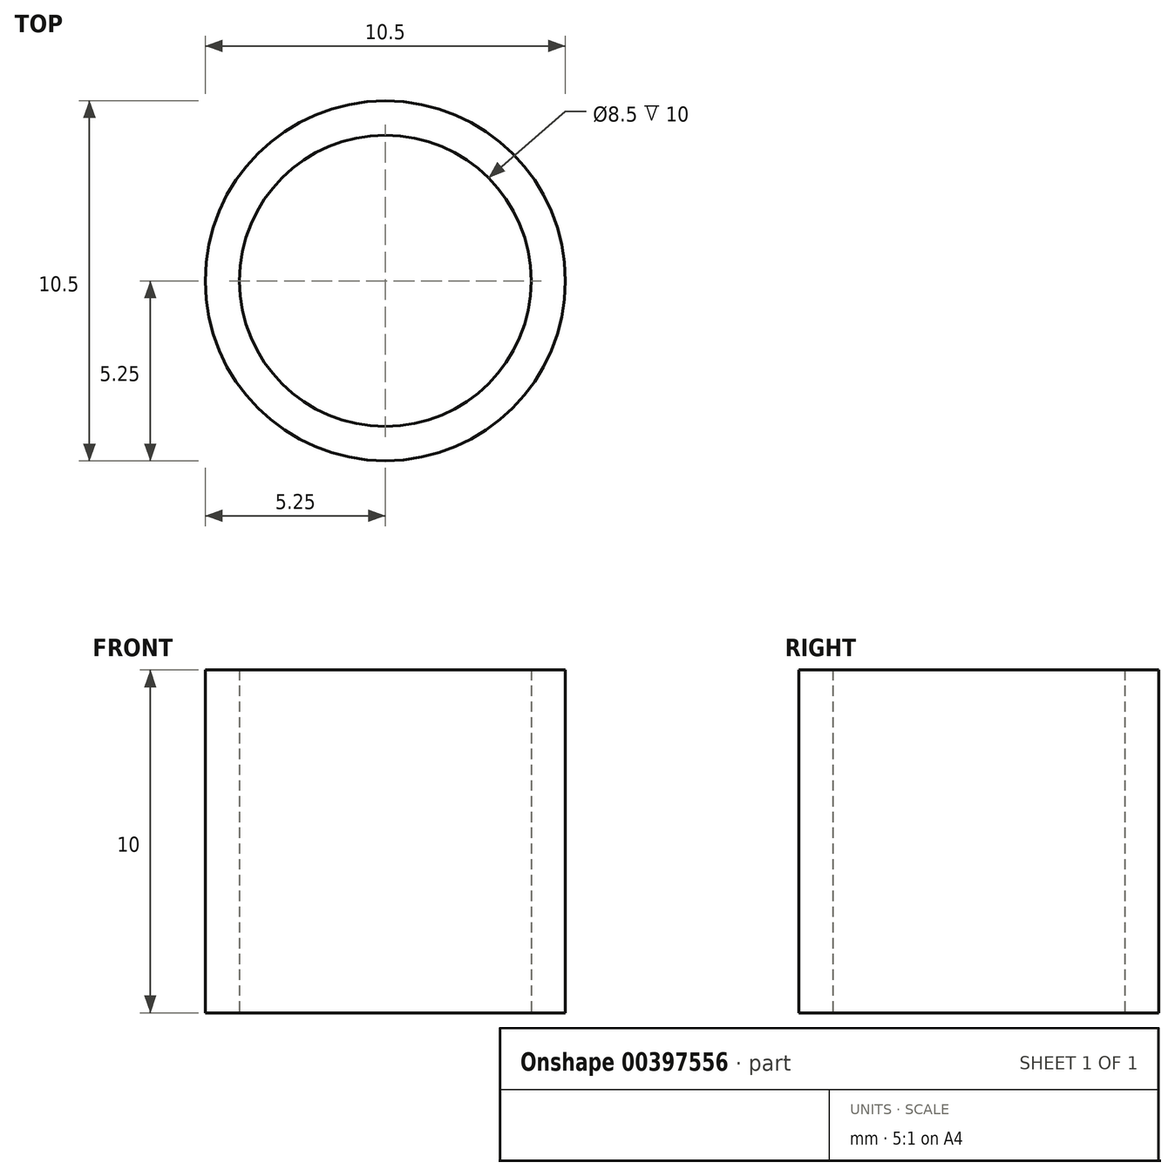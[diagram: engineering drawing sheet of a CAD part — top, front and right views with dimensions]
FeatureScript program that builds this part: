
annotation { "Feature Type Name" : "Feature", "Feature Type Description" : "" }
export const myFeature = defineFeature(function(context is Context, id is Id, definition is map)
    precondition{}
    {
        {
            var Q0;
            Q0=qCreatedBy(makeId("Top.planeOp"),FACE);
            var sketch = newSketch(context, id + "F0", { "sketchPlane" : qUnion([Q0])});
            skCircle(sketch, "E0", {"center": v(0, 0) * mm, "radius": 5.25 * mm});
            skCircle(sketch, "E1", {"center": v(0, 0) * mm, "radius": 4.25 * mm});
            skSolve(sketch);
        }
        {
            var Q0;
            Q0=makeQuery(id+"F0.imprint","IMPRINT",FACE,{"disambiguationData":[TD([[makeQuery(id+"F0.imprint","IMPRINT",EDGE,{"derivedFrom":sQuery(id+"F0.wireOp",EDGE,"E0")}),1.0]])]});
            extrude(context, id + "F1", {"entities" : qUnion([Q0]), "depth" : 10 * mm});
        }
    });
